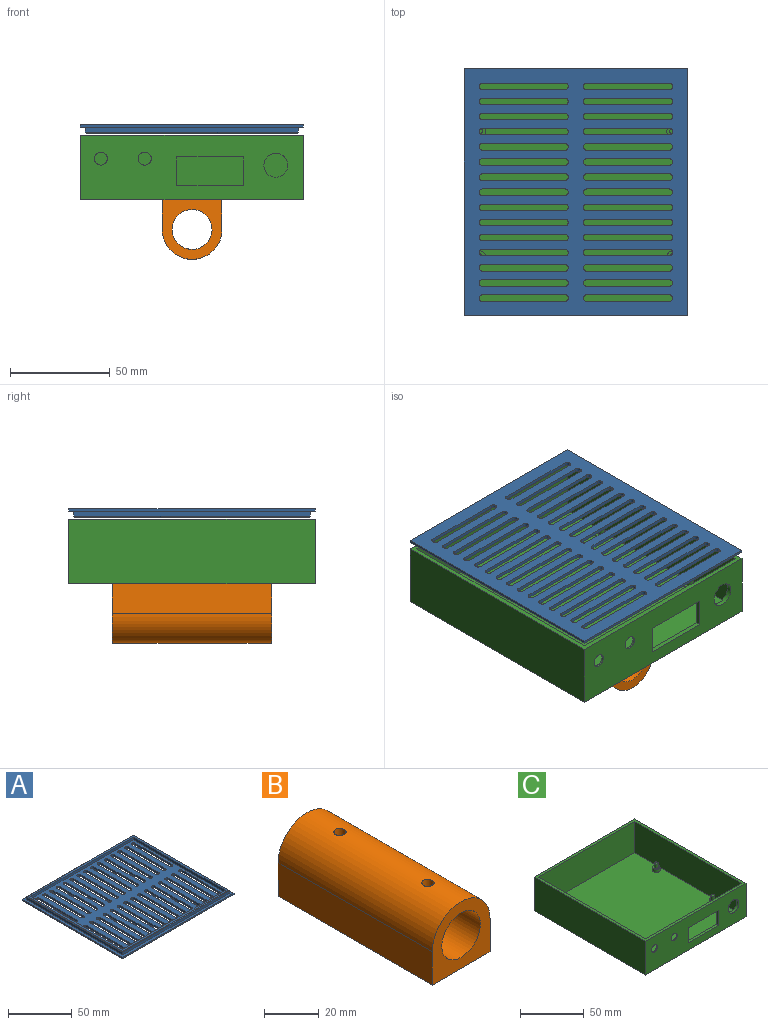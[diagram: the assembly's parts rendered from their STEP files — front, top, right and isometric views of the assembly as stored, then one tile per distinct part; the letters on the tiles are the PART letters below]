
ASSEMBLY  parts=3 mates=2
PART A: 260 faces, bbox 123.8x111.8x4.2 mm
  f0: plane 114x102mm, normal (0,0,1), area 7340.3mm2, adj f12,f13,f14,f15,f16,f17,f18,f19
  f1: plane 123.8x111.8mm, normal (0,0,-1), area 9553.2mm2, adj f4,f5,f6,f7,f16,f17,f18,f19
  f2: plane 117.8x105.8mm, normal (0,0,1), area 835.2mm2, adj f12,f13,f14,f15,f256,f257,f258,f259
  f3: plane 123.8x111.8mm, normal (0,0,1), area 1153mm2, adj f4,f5,f6,f7,f8,f9,f10,f11
  f4: plane 123.8x1.2mm, normal (0,-1,0), area 148.6mm2, adj f1,f3,f5,f7
  f5: plane 111.8x1.2mm, normal (1,0,0), area 134.2mm2, adj f1,f3,f4,f6
  f6: plane 123.8x1.2mm, normal (0,1,0), area 148.6mm2, adj f1,f3,f5,f7
  f7: plane 111.8x1.2mm, normal (-1,0,0), area 134.2mm2, adj f1,f3,f4,f6
  f8: plane 118.8x2.5mm, normal (0,1,0), area 297mm2, adj f3,f9,f11,f257
  f9: plane 106.8x2.5mm, normal (-1,0,0), area 267mm2, adj f3,f8,f10,f259
  f10: plane 118.8x2.5mm, normal (0,-1,0), area 297mm2, adj f3,f9,f11,f258
  f11: plane 106.8x2.5mm, normal (1,0,0), area 267mm2, adj f3,f8,f10,f256
  f12: plane 114x2.5mm, normal (0,-1,0), area 285mm2, adj f0,f2,f13,f15
  f13: plane 102x2.5mm, normal (1,0,0), area 255mm2, adj f0,f2,f12,f14
  f14: plane 114x2.5mm, normal (0,1,0), area 285mm2, adj f0,f2,f13,f15
  f15: plane 102x2.5mm, normal (-1,0,0), area 255mm2, adj f0,f2,f12,f14
  f16: plane 41.72x1.7mm, normal (-1,0,0), area 70.9mm2, adj f0,f1,f17,f23
  f17: cylinder r=1.4mm len=1.7mm, axis (0,0,1), area 3.7mm2, adj f0,f1,f16,f18
  f18: plane 1.7x0.45mm, normal (0,-1,0), area 0.8mm2, adj f0,f1,f17,f19
  f19: cylinder r=1.4mm len=1.7mm, axis (0,0,1), area 3.7mm2, adj f0,f1,f18,f20
  f20: plane 41.72x1.7mm, normal (1,0,0), area 70.9mm2, adj f0,f1,f19,f21
  f21: cylinder r=1.4mm len=1.7mm, axis (0,0,1), area 3.7mm2, adj f0,f1,f20,f22
  f22: plane 1.7x0.45mm, normal (0,1,0), area 0.8mm2, adj f0,f1,f21,f23
  f23: cylinder r=1.4mm len=1.7mm, axis (0,0,1), area 3.7mm2, adj f0,f1,f16,f22
  f24: plane 1.7x0.45mm, normal (0,1,0), area 0.8mm2, adj f0,f1,f25,f31
  f25: cylinder r=1.4mm len=1.7mm, axis (0,0,1), area 3.7mm2, adj f0,f1,f24,f26
  f26: plane 41.72x1.7mm, normal (-1,0,0), area 70.9mm2, adj f0,f1,f25,f27
  f27: cylinder r=1.4mm len=1.7mm, axis (0,0,1), area 3.7mm2, adj f0,f1,f26,f28
  f28: plane 1.7x0.45mm, normal (0,-1,0), area 0.8mm2, adj f0,f1,f27,f29
  f29: cylinder r=1.4mm len=1.7mm, axis (0,0,1), area 3.7mm2, adj f0,f1,f28,f30
  f30: plane 41.72x1.7mm, normal (1,0,0), area 70.9mm2, adj f0,f1,f29,f31
  f31: cylinder r=1.4mm len=1.7mm, axis (0,0,1), area 3.7mm2, adj f0,f1,f24,f30
  f32: cylinder r=1.4mm len=1.7mm, axis (0,0,1), area 3.7mm2, adj f0,f1,f33,f39
  f33: plane 41.72x1.7mm, normal (1,0,0), area 70.9mm2, adj f0,f1,f32,f34
  f34: cylinder r=1.4mm len=1.7mm, axis (0,0,1), area 3.7mm2, adj f0,f1,f33,f35
  f35: plane 1.7x0.45mm, normal (0,1,0), area 0.8mm2, adj f0,f1,f34,f36
  f36: cylinder r=1.4mm len=1.7mm, axis (0,0,1), area 3.7mm2, adj f0,f1,f35,f37
  f37: plane 41.72x1.7mm, normal (-1,0,0), area 70.9mm2, adj f0,f1,f36,f38
  f38: cylinder r=1.4mm len=1.7mm, axis (0,0,1), area 3.7mm2, adj f0,f1,f37,f39
  f39: plane 1.7x0.45mm, normal (0,-1,0), area 0.8mm2, adj f0,f1,f32,f38
  f40: plane 41.72x1.7mm, normal (1,0,0), area 70.9mm2, adj f0,f1,f41,f47
  f41: cylinder r=1.4mm len=1.7mm, axis (0,0,1), area 3.7mm2, adj f0,f1,f40,f42
  f42: plane 1.7x0.45mm, normal (0,1,0), area 0.8mm2, adj f0,f1,f41,f43
  f43: cylinder r=1.4mm len=1.7mm, axis (0,0,1), area 3.7mm2, adj f0,f1,f42,f44
  f44: plane 41.72x1.7mm, normal (-1,0,0), area 70.9mm2, adj f0,f1,f43,f45
  f45: cylinder r=1.4mm len=1.7mm, axis (0,0,1), area 3.7mm2, adj f0,f1,f44,f46
  f46: plane 1.7x0.45mm, normal (0,-1,0), area 0.8mm2, adj f0,f1,f45,f47
  f47: cylinder r=1.4mm len=1.7mm, axis (0,0,1), area 3.7mm2, adj f0,f1,f40,f46
  f48: cylinder r=1.4mm len=1.7mm, axis (0,0,1), area 3.7mm2, adj f0,f1,f49,f55
  f49: plane 41.72x1.7mm, normal (1,0,0), area 70.9mm2, adj f0,f1,f48,f50
  f50: cylinder r=1.4mm len=1.7mm, axis (0,0,1), area 3.7mm2, adj f0,f1,f49,f51
  f51: plane 1.7x0.45mm, normal (0,1,0), area 0.8mm2, adj f0,f1,f50,f52
  f52: cylinder r=1.4mm len=1.7mm, axis (0,0,1), area 3.7mm2, adj f0,f1,f51,f53
  f53: plane 41.72x1.7mm, normal (-1,0,0), area 70.9mm2, adj f0,f1,f52,f54
  f54: cylinder r=1.4mm len=1.7mm, axis (0,0,1), area 3.7mm2, adj f0,f1,f53,f55
  f55: plane 1.7x0.45mm, normal (0,-1,0), area 0.8mm2, adj f0,f1,f48,f54
  f56: plane 1.7x0.45mm, normal (0,1,0), area 0.8mm2, adj f0,f1,f57,f63
  f57: cylinder r=1.4mm len=1.7mm, axis (0,0,1), area 3.7mm2, adj f0,f1,f56,f58
  f58: plane 41.72x1.7mm, normal (-1,0,0), area 70.9mm2, adj f0,f1,f57,f59
  f59: cylinder r=1.4mm len=1.7mm, axis (0,0,1), area 3.7mm2, adj f0,f1,f58,f60
  f60: plane 1.7x0.45mm, normal (0,-1,0), area 0.8mm2, adj f0,f1,f59,f61
  f61: cylinder r=1.4mm len=1.7mm, axis (0,0,1), area 3.7mm2, adj f0,f1,f60,f62
  f62: plane 41.72x1.7mm, normal (1,0,0), area 70.9mm2, adj f0,f1,f61,f63
  f63: cylinder r=1.4mm len=1.7mm, axis (0,0,1), area 3.7mm2, adj f0,f1,f56,f62
  f64: cylinder r=1.4mm len=1.7mm, axis (0,0,1), area 3.7mm2, adj f0,f1,f65,f71
  f65: plane 41.72x1.7mm, normal (1,0,0), area 70.9mm2, adj f0,f1,f64,f66
  f66: cylinder r=1.4mm len=1.7mm, axis (0,0,1), area 3.7mm2, adj f0,f1,f65,f67
  f67: plane 1.7x0.45mm, normal (0,1,0), area 0.8mm2, adj f0,f1,f66,f68
  f68: cylinder r=1.4mm len=1.7mm, axis (0,0,1), area 3.7mm2, adj f0,f1,f67,f69
  f69: plane 41.72x1.7mm, normal (-1,0,0), area 70.9mm2, adj f0,f1,f68,f70
  f70: cylinder r=1.4mm len=1.7mm, axis (0,0,1), area 3.7mm2, adj f0,f1,f69,f71
  f71: plane 1.7x0.45mm, normal (0,-1,0), area 0.8mm2, adj f0,f1,f64,f70
  f72: plane 1.7x0.45mm, normal (0,1,0), area 0.8mm2, adj f0,f1,f73,f79
  f73: cylinder r=1.4mm len=1.7mm, axis (0,0,1), area 3.7mm2, adj f0,f1,f72,f74
  f74: plane 41.72x1.7mm, normal (-1,0,0), area 70.9mm2, adj f0,f1,f73,f75
  f75: cylinder r=1.4mm len=1.7mm, axis (0,0,1), area 3.7mm2, adj f0,f1,f74,f76
  f76: plane 1.7x0.45mm, normal (0,-1,0), area 0.8mm2, adj f0,f1,f75,f77
  f77: cylinder r=1.4mm len=1.7mm, axis (0,0,1), area 3.7mm2, adj f0,f1,f76,f78
  f78: plane 41.72x1.7mm, normal (1,0,0), area 70.9mm2, adj f0,f1,f77,f79
  f79: cylinder r=1.4mm len=1.7mm, axis (0,0,1), area 3.7mm2, adj f0,f1,f72,f78
  f80: cylinder r=1.4mm len=1.7mm, axis (0,0,1), area 3.7mm2, adj f0,f1,f81,f87
  f81: plane 41.72x1.7mm, normal (1,0,0), area 70.9mm2, adj f0,f1,f80,f82
  f82: cylinder r=1.4mm len=1.7mm, axis (0,0,1), area 3.7mm2, adj f0,f1,f81,f83
  f83: plane 1.7x0.45mm, normal (0,1,0), area 0.8mm2, adj f0,f1,f82,f84
  f84: cylinder r=1.4mm len=1.7mm, axis (0,0,1), area 3.7mm2, adj f0,f1,f83,f85
  f85: plane 41.72x1.7mm, normal (-1,0,0), area 70.9mm2, adj f0,f1,f84,f86
  f86: cylinder r=1.4mm len=1.7mm, axis (0,0,1), area 3.7mm2, adj f0,f1,f85,f87
  f87: plane 1.7x0.45mm, normal (0,-1,0), area 0.8mm2, adj f0,f1,f80,f86
  f88: plane 41.72x1.7mm, normal (1,0,0), area 70.9mm2, adj f0,f1,f89,f95
  f89: cylinder r=1.4mm len=1.7mm, axis (0,0,1), area 3.7mm2, adj f0,f1,f88,f90
  f90: plane 1.7x0.45mm, normal (0,1,0), area 0.8mm2, adj f0,f1,f89,f91
  f91: cylinder r=1.4mm len=1.7mm, axis (0,0,1), area 3.7mm2, adj f0,f1,f90,f92
  f92: plane 41.72x1.7mm, normal (-1,0,0), area 70.9mm2, adj f0,f1,f91,f93
  f93: cylinder r=1.4mm len=1.7mm, axis (0,0,1), area 3.7mm2, adj f0,f1,f92,f94
  f94: plane 1.7x0.45mm, normal (0,-1,0), area 0.8mm2, adj f0,f1,f93,f95
  f95: cylinder r=1.4mm len=1.7mm, axis (0,0,1), area 3.7mm2, adj f0,f1,f88,f94
  f96: plane 1.7x0.45mm, normal (0,1,0), area 0.8mm2, adj f0,f1,f97,f103
  f97: cylinder r=1.4mm len=1.7mm, axis (0,0,1), area 3.7mm2, adj f0,f1,f96,f98
  f98: plane 41.72x1.7mm, normal (-1,0,0), area 70.9mm2, adj f0,f1,f97,f99
  f99: cylinder r=1.4mm len=1.7mm, axis (0,0,1), area 3.7mm2, adj f0,f1,f98,f100
  f100: plane 1.7x0.45mm, normal (0,-1,0), area 0.8mm2, adj f0,f1,f99,f101
  f101: cylinder r=1.4mm len=1.7mm, axis (0,0,1), area 3.7mm2, adj f0,f1,f100,f102
  f102: plane 41.72x1.7mm, normal (1,0,0), area 70.9mm2, adj f0,f1,f101,f103
  f103: cylinder r=1.4mm len=1.7mm, axis (0,0,1), area 3.7mm2, adj f0,f1,f96,f102
  f104: cylinder r=1.4mm len=1.7mm, axis (0,0,1), area 3.7mm2, adj f0,f1,f105,f111
  f105: plane 41.72x1.7mm, normal (1,0,0), area 70.9mm2, adj f0,f1,f104,f106
  f106: cylinder r=1.4mm len=1.7mm, axis (0,0,1), area 3.7mm2, adj f0,f1,f105,f107
  f107: plane 1.7x0.45mm, normal (0,1,0), area 0.8mm2, adj f0,f1,f106,f108
  f108: cylinder r=1.4mm len=1.7mm, axis (0,0,1), area 3.7mm2, adj f0,f1,f107,f109
  f109: plane 41.72x1.7mm, normal (-1,0,0), area 70.9mm2, adj f0,f1,f108,f110
  f110: cylinder r=1.4mm len=1.7mm, axis (0,0,1), area 3.7mm2, adj f0,f1,f109,f111
  f111: plane 1.7x0.45mm, normal (0,-1,0), area 0.8mm2, adj f0,f1,f104,f110
  f112: plane 1.7x0.45mm, normal (0,1,0), area 0.8mm2, adj f0,f1,f113,f119
  f113: cylinder r=1.4mm len=1.7mm, axis (0,0,1), area 3.7mm2, adj f0,f1,f112,f114
  f114: plane 41.72x1.7mm, normal (-1,0,0), area 70.9mm2, adj f0,f1,f113,f115
  f115: cylinder r=1.4mm len=1.7mm, axis (0,0,1), area 3.7mm2, adj f0,f1,f114,f116
  f116: plane 1.7x0.45mm, normal (0,-1,0), area 0.8mm2, adj f0,f1,f115,f117
  f117: cylinder r=1.4mm len=1.7mm, axis (0,0,1), area 3.7mm2, adj f0,f1,f116,f118
  f118: plane 41.72x1.7mm, normal (1,0,0), area 70.9mm2, adj f0,f1,f117,f119
  f119: cylinder r=1.4mm len=1.7mm, axis (0,0,1), area 3.7mm2, adj f0,f1,f112,f118
  f120: plane 1.7x0.45mm, normal (0,-1,0), area 0.8mm2, adj f0,f1,f121,f127
  f121: cylinder r=1.4mm len=1.7mm, axis (0,0,1), area 3.7mm2, adj f0,f1,f120,f122
  f122: plane 41.72x1.7mm, normal (1,0,0), area 70.9mm2, adj f0,f1,f121,f123
  f123: cylinder r=1.4mm len=1.7mm, axis (0,0,1), area 3.7mm2, adj f0,f1,f122,f124
  f124: plane 1.7x0.45mm, normal (0,1,0), area 0.8mm2, adj f0,f1,f123,f125
  f125: cylinder r=1.4mm len=1.7mm, axis (0,0,1), area 3.7mm2, adj f0,f1,f124,f126
  f126: plane 41.72x1.7mm, normal (-1,0,0), area 70.9mm2, adj f0,f1,f125,f127
  f127: cylinder r=1.4mm len=1.7mm, axis (0,0,1), area 3.7mm2, adj f0,f1,f120,f126
  f128: plane 41.72x1.7mm, normal (1,0,0), area 70.9mm2, adj f0,f1,f129,f135
  f129: cylinder r=1.4mm len=1.7mm, axis (0,0,1), area 3.7mm2, adj f0,f1,f128,f130
  f130: plane 1.7x0.45mm, normal (0,1,0), area 0.8mm2, adj f0,f1,f129,f131
  f131: cylinder r=1.4mm len=1.7mm, axis (0,0,1), area 3.7mm2, adj f0,f1,f130,f132
  f132: plane 41.72x1.7mm, normal (-1,0,0), area 70.9mm2, adj f0,f1,f131,f133
  f133: cylinder r=1.4mm len=1.7mm, axis (0,0,1), area 3.7mm2, adj f0,f1,f132,f134
  f134: plane 1.7x0.45mm, normal (0,-1,0), area 0.8mm2, adj f0,f1,f133,f135
  f135: cylinder r=1.4mm len=1.7mm, axis (0,0,1), area 3.7mm2, adj f0,f1,f128,f134
  f136: plane 1.7x0.45mm, normal (0,-1,0), area 0.8mm2, adj f0,f1,f137,f143
  f137: cylinder r=1.4mm len=1.7mm, axis (0,0,1), area 3.7mm2, adj f0,f1,f136,f138
  f138: plane 41.72x1.7mm, normal (1,0,0), area 70.9mm2, adj f0,f1,f137,f139
  f139: cylinder r=1.4mm len=1.7mm, axis (0,0,1), area 3.7mm2, adj f0,f1,f138,f140
  f140: plane 1.7x0.45mm, normal (0,1,0), area 0.8mm2, adj f0,f1,f139,f141
  f141: cylinder r=1.4mm len=1.7mm, axis (0,0,1), area 3.7mm2, adj f0,f1,f140,f142
  f142: plane 41.72x1.7mm, normal (-1,0,0), area 70.9mm2, adj f0,f1,f141,f143
  f143: cylinder r=1.4mm len=1.7mm, axis (0,0,1), area 3.7mm2, adj f0,f1,f136,f142
  f144: plane 41.72x1.7mm, normal (1,0,0), area 70.9mm2, adj f0,f1,f145,f151
  f145: cylinder r=1.4mm len=1.7mm, axis (0,0,1), area 3.7mm2, adj f0,f1,f144,f146
  f146: plane 1.7x0.45mm, normal (0,1,0), area 0.8mm2, adj f0,f1,f145,f147
  f147: cylinder r=1.4mm len=1.7mm, axis (0,0,1), area 3.7mm2, adj f0,f1,f146,f148
  f148: plane 41.72x1.7mm, normal (-1,0,0), area 70.9mm2, adj f0,f1,f147,f149
  f149: cylinder r=1.4mm len=1.7mm, axis (0,0,1), area 3.7mm2, adj f0,f1,f148,f150
  f150: plane 1.7x0.45mm, normal (0,-1,0), area 0.8mm2, adj f0,f1,f149,f151
  f151: cylinder r=1.4mm len=1.7mm, axis (0,0,1), area 3.7mm2, adj f0,f1,f144,f150
  f152: cylinder r=1.4mm len=1.7mm, axis (0,0,1), area 3.7mm2, adj f0,f1,f153,f159
  f153: plane 41.72x1.7mm, normal (1,0,0), area 70.9mm2, adj f0,f1,f152,f154
  f154: cylinder r=1.4mm len=1.7mm, axis (0,0,1), area 3.7mm2, adj f0,f1,f153,f155
  f155: plane 1.7x0.45mm, normal (0,1,0), area 0.8mm2, adj f0,f1,f154,f156
  f156: cylinder r=1.4mm len=1.7mm, axis (0,0,1), area 3.7mm2, adj f0,f1,f155,f157
  f157: plane 41.72x1.7mm, normal (-1,0,0), area 70.9mm2, adj f0,f1,f156,f158
  f158: cylinder r=1.4mm len=1.7mm, axis (0,0,1), area 3.7mm2, adj f0,f1,f157,f159
  f159: plane 1.7x0.45mm, normal (0,-1,0), area 0.8mm2, adj f0,f1,f152,f158
  f160: plane 41.72x1.7mm, normal (1,0,0), area 70.9mm2, adj f0,f1,f161,f167
  f161: cylinder r=1.4mm len=1.7mm, axis (0,0,1), area 3.7mm2, adj f0,f1,f160,f162
  f162: plane 1.7x0.45mm, normal (0,1,0), area 0.8mm2, adj f0,f1,f161,f163
  f163: cylinder r=1.4mm len=1.7mm, axis (0,0,1), area 3.7mm2, adj f0,f1,f162,f164
  f164: plane 41.72x1.7mm, normal (-1,0,0), area 70.9mm2, adj f0,f1,f163,f165
  f165: cylinder r=1.4mm len=1.7mm, axis (0,0,1), area 3.7mm2, adj f0,f1,f164,f166
  f166: plane 1.7x0.45mm, normal (0,-1,0), area 0.8mm2, adj f0,f1,f165,f167
  f167: cylinder r=1.4mm len=1.7mm, axis (0,0,1), area 3.7mm2, adj f0,f1,f160,f166
  f168: plane 1.7x0.45mm, normal (0,-1,0), area 0.8mm2, adj f0,f1,f169,f175
  f169: cylinder r=1.4mm len=1.7mm, axis (0,0,1), area 3.7mm2, adj f0,f1,f168,f170
  f170: plane 41.72x1.7mm, normal (1,0,0), area 70.9mm2, adj f0,f1,f169,f171
  f171: cylinder r=1.4mm len=1.7mm, axis (0,0,1), area 3.7mm2, adj f0,f1,f170,f172
  f172: plane 1.7x0.45mm, normal (0,1,0), area 0.8mm2, adj f0,f1,f171,f173
  f173: cylinder r=1.4mm len=1.7mm, axis (0,0,1), area 3.7mm2, adj f0,f1,f172,f174
  f174: plane 41.72x1.7mm, normal (-1,0,0), area 70.9mm2, adj f0,f1,f173,f175
  f175: cylinder r=1.4mm len=1.7mm, axis (0,0,1), area 3.7mm2, adj f0,f1,f168,f174
  f176: plane 41.72x1.7mm, normal (1,0,0), area 70.9mm2, adj f0,f1,f177,f183
  f177: cylinder r=1.4mm len=1.7mm, axis (0,0,1), area 3.7mm2, adj f0,f1,f176,f178
  f178: plane 1.7x0.45mm, normal (0,1,0), area 0.8mm2, adj f0,f1,f177,f179
  f179: cylinder r=1.4mm len=1.7mm, axis (0,0,1), area 3.7mm2, adj f0,f1,f178,f180
  f180: plane 41.72x1.7mm, normal (-1,0,0), area 70.9mm2, adj f0,f1,f179,f181
  f181: cylinder r=1.4mm len=1.7mm, axis (0,0,1), area 3.7mm2, adj f0,f1,f180,f182
  f182: plane 1.7x0.45mm, normal (0,-1,0), area 0.8mm2, adj f0,f1,f181,f183
  f183: cylinder r=1.4mm len=1.7mm, axis (0,0,1), area 3.7mm2, adj f0,f1,f176,f182
  f184: plane 1.7x0.45mm, normal (0,-1,0), area 0.8mm2, adj f0,f1,f185,f191
  f185: cylinder r=1.4mm len=1.7mm, axis (0,0,1), area 3.7mm2, adj f0,f1,f184,f186
  f186: plane 41.72x1.7mm, normal (1,0,0), area 70.9mm2, adj f0,f1,f185,f187
  f187: cylinder r=1.4mm len=1.7mm, axis (0,0,1), area 3.7mm2, adj f0,f1,f186,f188
  f188: plane 1.7x0.45mm, normal (0,1,0), area 0.8mm2, adj f0,f1,f187,f189
  f189: cylinder r=1.4mm len=1.7mm, axis (0,0,1), area 3.7mm2, adj f0,f1,f188,f190
  f190: plane 41.72x1.7mm, normal (-1,0,0), area 70.9mm2, adj f0,f1,f189,f191
  f191: cylinder r=1.4mm len=1.7mm, axis (0,0,1), area 3.7mm2, adj f0,f1,f184,f190
  f192: plane 1.7x0.45mm, normal (0,1,0), area 0.8mm2, adj f0,f1,f193,f199
  f193: cylinder r=1.4mm len=1.7mm, axis (0,0,1), area 3.7mm2, adj f0,f1,f192,f194
  f194: plane 41.72x1.7mm, normal (-1,0,0), area 70.9mm2, adj f0,f1,f193,f195
  f195: cylinder r=1.4mm len=1.7mm, axis (0,0,1), area 3.7mm2, adj f0,f1,f194,f196
  f196: plane 1.7x0.45mm, normal (0,-1,0), area 0.8mm2, adj f0,f1,f195,f197
  f197: cylinder r=1.4mm len=1.7mm, axis (0,0,1), area 3.7mm2, adj f0,f1,f196,f198
  f198: plane 41.72x1.7mm, normal (1,0,0), area 70.9mm2, adj f0,f1,f197,f199
  f199: cylinder r=1.4mm len=1.7mm, axis (0,0,1), area 3.7mm2, adj f0,f1,f192,f198
  f200: cylinder r=1.4mm len=1.7mm, axis (0,0,1), area 3.7mm2, adj f0,f1,f201,f207
  f201: plane 41.72x1.7mm, normal (1,0,0), area 70.9mm2, adj f0,f1,f200,f202
  f202: cylinder r=1.4mm len=1.7mm, axis (0,0,1), area 3.7mm2, adj f0,f1,f201,f203
  f203: plane 1.7x0.45mm, normal (0,1,0), area 0.8mm2, adj f0,f1,f202,f204
  f204: cylinder r=1.4mm len=1.7mm, axis (0,0,1), area 3.7mm2, adj f0,f1,f203,f205
  f205: plane 41.72x1.7mm, normal (-1,0,0), area 70.9mm2, adj f0,f1,f204,f206
  f206: cylinder r=1.4mm len=1.7mm, axis (0,0,1), area 3.7mm2, adj f0,f1,f205,f207
  f207: plane 1.7x0.45mm, normal (0,-1,0), area 0.8mm2, adj f0,f1,f200,f206
  f208: plane 41.72x1.7mm, normal (1,0,0), area 70.9mm2, adj f0,f1,f209,f215
  f209: cylinder r=1.4mm len=1.7mm, axis (0,0,1), area 3.7mm2, adj f0,f1,f208,f210
  f210: plane 1.7x0.45mm, normal (0,1,0), area 0.8mm2, adj f0,f1,f209,f211
  f211: cylinder r=1.4mm len=1.7mm, axis (0,0,1), area 3.7mm2, adj f0,f1,f210,f212
  f212: plane 41.72x1.7mm, normal (-1,0,0), area 70.9mm2, adj f0,f1,f211,f213
  f213: cylinder r=1.4mm len=1.7mm, axis (0,0,1), area 3.7mm2, adj f0,f1,f212,f214
  f214: plane 1.7x0.45mm, normal (0,-1,0), area 0.8mm2, adj f0,f1,f213,f215
  f215: cylinder r=1.4mm len=1.7mm, axis (0,0,1), area 3.7mm2, adj f0,f1,f208,f214
  f216: cylinder r=1.4mm len=1.7mm, axis (0,0,1), area 3.7mm2, adj f0,f1,f217,f223
  f217: plane 41.72x1.7mm, normal (1,0,0), area 70.9mm2, adj f0,f1,f216,f218
  f218: cylinder r=1.4mm len=1.7mm, axis (0,0,1), area 3.7mm2, adj f0,f1,f217,f219
  f219: plane 1.7x0.45mm, normal (0,1,0), area 0.8mm2, adj f0,f1,f218,f220
  f220: cylinder r=1.4mm len=1.7mm, axis (0,0,1), area 3.7mm2, adj f0,f1,f219,f221
  f221: plane 41.72x1.7mm, normal (-1,0,0), area 70.9mm2, adj f0,f1,f220,f222
  f222: cylinder r=1.4mm len=1.7mm, axis (0,0,1), area 3.7mm2, adj f0,f1,f221,f223
  f223: plane 1.7x0.45mm, normal (0,-1,0), area 0.8mm2, adj f0,f1,f216,f222
  f224: plane 1.7x0.45mm, normal (0,1,0), area 0.8mm2, adj f0,f1,f225,f231
  f225: cylinder r=1.4mm len=1.7mm, axis (0,0,1), area 3.7mm2, adj f0,f1,f224,f226
  f226: plane 41.72x1.7mm, normal (-1,0,0), area 70.9mm2, adj f0,f1,f225,f227
  f227: cylinder r=1.4mm len=1.7mm, axis (0,0,1), area 3.7mm2, adj f0,f1,f226,f228
  f228: plane 1.7x0.45mm, normal (0,-1,0), area 0.8mm2, adj f0,f1,f227,f229
  f229: cylinder r=1.4mm len=1.7mm, axis (0,0,1), area 3.7mm2, adj f0,f1,f228,f230
  f230: plane 41.72x1.7mm, normal (1,0,0), area 70.9mm2, adj f0,f1,f229,f231
  f231: cylinder r=1.4mm len=1.7mm, axis (0,0,1), area 3.7mm2, adj f0,f1,f224,f230
  f232: cylinder r=1.4mm len=1.7mm, axis (0,0,1), area 3.7mm2, adj f0,f1,f233,f239
  f233: plane 41.72x1.7mm, normal (1,0,0), area 70.9mm2, adj f0,f1,f232,f234
  f234: cylinder r=1.4mm len=1.7mm, axis (0,0,1), area 3.7mm2, adj f0,f1,f233,f235
  f235: plane 1.7x0.45mm, normal (0,1,0), area 0.8mm2, adj f0,f1,f234,f236
  f236: cylinder r=1.4mm len=1.7mm, axis (0,0,1), area 3.7mm2, adj f0,f1,f235,f237
  f237: plane 41.72x1.7mm, normal (-1,0,0), area 70.9mm2, adj f0,f1,f236,f238
  f238: cylinder r=1.4mm len=1.7mm, axis (0,0,1), area 3.7mm2, adj f0,f1,f237,f239
  f239: plane 1.7x0.45mm, normal (0,-1,0), area 0.8mm2, adj f0,f1,f232,f238
  f240: plane 1.7x0.45mm, normal (0,1,0), area 0.8mm2, adj f0,f1,f241,f247
  f241: cylinder r=1.4mm len=1.7mm, axis (0,0,1), area 3.7mm2, adj f0,f1,f240,f242
  f242: plane 41.72x1.7mm, normal (-1,0,0), area 70.9mm2, adj f0,f1,f241,f243
  f243: cylinder r=1.4mm len=1.7mm, axis (0,0,1), area 3.7mm2, adj f0,f1,f242,f244
  f244: plane 1.7x0.45mm, normal (0,-1,0), area 0.8mm2, adj f0,f1,f243,f245
  f245: cylinder r=1.4mm len=1.7mm, axis (0,0,1), area 3.7mm2, adj f0,f1,f244,f246
  f246: plane 41.72x1.7mm, normal (1,0,0), area 70.9mm2, adj f0,f1,f245,f247
  f247: cylinder r=1.4mm len=1.7mm, axis (0,0,1), area 3.7mm2, adj f0,f1,f240,f246
  f248: cylinder r=1.4mm len=1.7mm, axis (0,0,1), area 3.7mm2, adj f0,f1,f249,f255
  f249: plane 41.72x1.7mm, normal (1,0,0), area 70.9mm2, adj f0,f1,f248,f250
  f250: cylinder r=1.4mm len=1.7mm, axis (0,0,1), area 3.7mm2, adj f0,f1,f249,f251
  f251: plane 1.7x0.45mm, normal (0,1,0), area 0.8mm2, adj f0,f1,f250,f252
  f252: cylinder r=1.4mm len=1.7mm, axis (0,0,1), area 3.7mm2, adj f0,f1,f251,f253
  f253: plane 41.72x1.7mm, normal (-1,0,0), area 70.9mm2, adj f0,f1,f252,f254
  f254: cylinder r=1.4mm len=1.7mm, axis (0,0,1), area 3.7mm2, adj f0,f1,f253,f255
  f255: plane 1.7x0.45mm, normal (0,-1,0), area 0.8mm2, adj f0,f1,f248,f254
  f256: plane 106.8x0.5mm, normal (0.71,0,0.71), area 75.2mm2, adj f2,f11,f257,f258
  f257: plane 118.8x0.5mm, normal (0,0.71,0.71), area 83.7mm2, adj f2,f8,f256,f259
  f258: plane 118.8x0.5mm, normal (0,-0.71,0.71), area 83.7mm2, adj f2,f10,f256,f259
  f259: plane 106.8x0.5mm, normal (-0.71,0,0.71), area 75.2mm2, adj f2,f9,f257,f258
PART B: 9 faces, bbox 30x80x30 mm
  f0: cylinder r=15mm len=80mm, axis (0,1,0), area 3738mm2, adj f3,f4,f5,f6,f7,f8
  f1: cylinder r=10mm len=80mm, axis (0,1,0), area 4994.6mm2, adj f5,f6,f7,f8
  f2: plane 80x30mm, normal (0,0,-1), area 2400mm2, adj f3,f4,f5,f6
  f3: plane 80x15mm, normal (1,0,0), area 1200mm2, adj f0,f2,f5,f6
  f4: plane 80x15mm, normal (-1,0,0), area 1200mm2, adj f0,f2,f5,f6
  f5: plane 30x30mm, normal (0,-1,0), area 489.3mm2, adj f0,f1,f2,f3,f4
  f6: plane 30x30mm, normal (0,1,0), area 489.3mm2, adj f0,f1,f2,f3,f4
  f7: cylinder r=2.25mm len=5.26mm, axis (0,0,-1), area 71.3mm2, adj f0,f1
  f8: cylinder r=2.25mm len=5.26mm, axis (0,0,-1), area 71.3mm2, adj f0,f1
PART C: 38 faces, bbox 111.8x123.8x32.4 mm
  f0: cylinder r=3.3mm len=6.6mm, axis (0,-1,0), area 18.7mm2, adj f2,f36
  f1: cylinder r=3.3mm len=6.6mm, axis (0,-1,0), area 18.7mm2, adj f2,f34
  f2: plane 111.8x32.4mm, normal (0,-1,0), area 2955mm2, adj f0,f1,f4,f6,f7,f8,f29,f30
  f3: plane 107x30mm, normal (0,1,0), area 2246.8mm2, adj f4,f10,f11,f12,f29,f30,f31,f32
  f4: plane 123.8x111.8mm, normal (0,0,1), area 1107.8mm2, adj f2,f3,f5,f6,f7,f9,f10,f11
  f5: plane 111.8x32.4mm, normal (0,1,0), area 3622.3mm2, adj f4,f6,f7,f8
  f6: plane 123.8x32.4mm, normal (-1,0,0), area 4011.1mm2, adj f2,f4,f5,f8
  f7: plane 123.8x32.4mm, normal (1,0,0), area 4011.1mm2, adj f2,f4,f5,f8
  f8: plane 123.8x111.8mm, normal (0,0,-1), area 13840.8mm2, adj f2,f5,f6,f7
  f9: plane 107x30mm, normal (0,-1,0), area 3210mm2, adj f4,f10,f11,f12
  f10: plane 119x30mm, normal (1,0,0), area 3570mm2, adj f3,f4,f9,f12
  f11: plane 119x30mm, normal (-1,0,0), area 3570mm2, adj f3,f4,f9,f12
  f12: plane 119x107mm, normal (0,0,1), area 12619.9mm2, adj f3,f9,f10,f11,f13,f15,f17,f19
  f13: cylinder r=3mm len=6mm, axis (0,0,-1), area 56.5mm2, adj f12,f14
  f14: plane 6x6mm, normal (0,0,1), area 21.2mm2, adj f13,f21
  f15: cylinder r=3mm len=6mm, axis (0,0,-1), area 56.5mm2, adj f12,f16
  f16: plane 6x6mm, normal (0,0,1), area 21.2mm2, adj f15,f25
  f17: cylinder r=3mm len=6mm, axis (0,0,-1), area 56.5mm2, adj f12,f18
  f18: plane 6x6mm, normal (0,0,1), area 21.2mm2, adj f17,f23
  f19: cylinder r=3mm len=6mm, axis (0,0,-1), area 56.5mm2, adj f12,f20
  f20: plane 6x6mm, normal (0,0,1), area 21.2mm2, adj f19,f27
  f21: cylinder r=1.5mm len=4mm, axis (0,0,-1), area 37.7mm2, adj f14,f22
  f22: plane 3x3mm, normal (0,0,1), area 7.1mm2, adj f21
  f23: cylinder r=1.5mm len=4mm, axis (0,0,-1), area 37.7mm2, adj f18,f24
  f24: plane 3x3mm, normal (0,0,1), area 7.1mm2, adj f23
  f25: cylinder r=1.5mm len=4mm, axis (0,0,-1), area 37.7mm2, adj f16,f26
  f26: plane 3x3mm, normal (0,0,1), area 7.1mm2, adj f25
  f27: cylinder r=1.5mm len=4mm, axis (0,0,-1), area 37.7mm2, adj f20,f28
  f28: plane 3x3mm, normal (0,0,1), area 7.1mm2, adj f27
  f29: plane 33.5x2.4mm, normal (0,0,1), area 80.4mm2, adj f2,f3,f30,f32
  f30: plane 14.5x2.4mm, normal (-1,0,0), area 34.8mm2, adj f2,f3,f29,f31
  f31: plane 33.5x2.4mm, normal (0,0,-1), area 80.4mm2, adj f2,f3,f30,f32
  f32: plane 14.5x2.4mm, normal (1,0,0), area 34.8mm2, adj f2,f3,f29,f31
  f33: cylinder r=6mm len=12mm, axis (0,-1,0), area 90.5mm2, adj f2,f3
  f34: plane 15.06x15.06mm, normal (0,1,0), area 143.9mm2, adj f1,f35
  f35: cylinder r=7.53mm len=15.06mm, axis (0,1,0), area 71mm2, adj f3,f34
  f36: plane 15.4x15.4mm, normal (0,1,0), area 152mm2, adj f0,f37
  f37: cylinder r=7.7mm len=15.4mm, axis (0,1,0), area 72.6mm2, adj f3,f36
PLACE A rot(axis=(0.71,0.71,0),180deg) t=(1.29,4.02,39.41)mm
PLACE B rot(axis=(0,1,0),180deg) t=(1.39,4.12,-13.19)mm
PLACE C rot(axis=(0,0,1),0deg) t=(1.39,4.12,4.21)mm
MATE planar B.f2 <-> C.f8  axis (0,0,1) through (1.39,4.12,1.81)mm
MATE planar A.f9 <-> C.f3  axis (0,-1,0) through (-52.11,-55.38,38.21)mm
